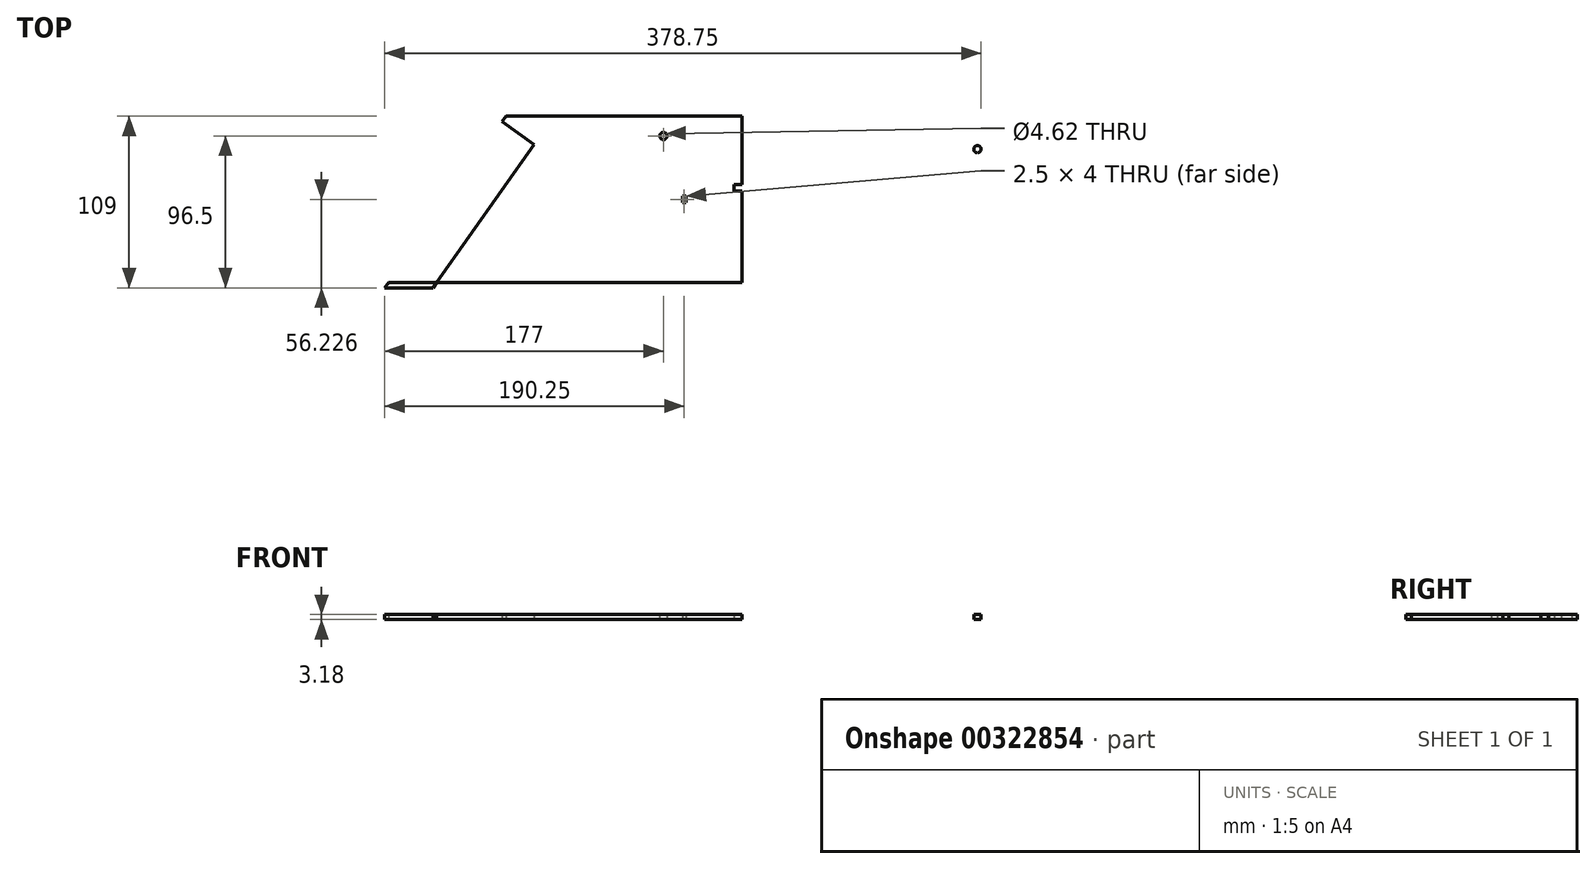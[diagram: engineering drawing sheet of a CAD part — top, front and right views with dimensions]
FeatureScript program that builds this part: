
annotation { "Feature Type Name" : "Feature", "Feature Type Description" : "" }
export const myFeature = defineFeature(function(context is Context, id is Id, definition is map)
    precondition{}
    {
        {
            var Q0;
            Q0=qCreatedBy(makeId("Top.planeOp"),FACE);
            var sketch = newSketch(context, id + "F0", { "sketchPlane" : qUnion([Q0])});
            skLineSegment(sketch, "E0.bottom", {"start": v(-423.4, 0) * mm, "end": v(-454, 0) * mm});
            skLineSegment(sketch, "E0.top", {"start": v(0, 109) * mm, "end": v(-454, 109) * mm});
            skLineSegment(sketch, "E0.left", {"start": v(0, 0) * mm, "end": v(0, 109) * mm});
            skLineSegment(sketch, "E0.right", {"start": v(-454, 0) * mm, "end": v(-454, 109) * mm});
            skLineSegment(sketch, "E1", {"start": v(-227, 109) * mm, "end": v(-77, 109) * mm});
            skLineSegment(sketch, "E2", {"start": v(-77, 109) * mm, "end": v(0, 0) * mm});
            skLineSegment(sketch, "E3", {"start": v(-227, 109) * mm, "end": v(-377, 109) * mm});
            skLineSegment(sketch, "E4", {"start": v(-377, 109) * mm, "end": v(-454, 0) * mm});
            skLineSegment(sketch, "E5.bottom", {"start": v(-177, 96.5) * mm, "end": v(-179.31, 96.5) * mm});
            skLineSegment(sketch, "E5.top", {"start": v(-177, 121.5) * mm, "end": v(-277, 121.5) * mm});
            skLineSegment(sketch, "E5.left", {"start": v(-177, 96.5) * mm, "end": v(-177, 98.81) * mm});
            skLineSegment(sketch, "E5.right", {"start": v(-277, 96.5) * mm, "end": v(-277, 98.81) * mm});
            skPoint(sketch, "E5.middle", {"position": v(-227, 109) * mm});
            skCircle(sketch, "E6", {"center": v(-277, 96.5) * mm, "radius": 2.31 * mm});
            skCircle(sketch, "E7", {"center": v(-177, 96.5) * mm, "radius": 2.31 * mm});
            skLineSegment(sketch, "E8.trimOffspring", {"start": v(-274.69, 96.5) * mm, "end": v(-277, 96.5) * mm});
            skLineSegment(sketch, "E9.trimOffspring", {"start": v(-277, 109) * mm, "end": v(-277, 121.5) * mm});
            skLineSegment(sketch, "E10.trimOffspring", {"start": v(-177, 109) * mm, "end": v(-177, 121.5) * mm});
            skLineSegment(sketch, "E11", {"start": v(-415.5, 54.5) * mm, "end": v(-386.65, 95.34) * mm});
            skLineSegment(sketch, "E12", {"start": v(-386.65, 95.34) * mm, "end": v(-435.7, 25.91) * mm});
            skLineSegment(sketch, "E13", {"start": v(-435.7, 25.91) * mm, "end": v(-425.48, 18.7) * mm});
            skLineSegment(sketch, "E14", {"start": v(-425.48, 18.7) * mm, "end": v(-376.44, 88.13) * mm});
            skLineSegment(sketch, "E15", {"start": v(-376.44, 88.13) * mm, "end": v(-386.65, 95.34) * mm});
            skCircle(sketch, "E16", {"center": v(-425.48, 18.7) * mm, "radius": 2.31 * mm});
            skCircle(sketch, "E17", {"center": v(-376.44, 88.13) * mm, "radius": 2.31 * mm});
            skLineSegment(sketch, "E18", {"start": v(-386.65, 95.34) * mm, "end": v(-379.44, 105.55) * mm});
            skLineSegment(sketch, "E19", {"start": v(-379.44, 105.55) * mm, "end": v(-359.02, 91.12) * mm});
            skLineSegment(sketch, "E20", {"start": v(-359.02, 91.12) * mm, "end": v(-423.4, 0) * mm});
            skLineSegment(sketch, "E21", {"start": v(-227, 109) * mm, "end": v(-227, 77.21) * mm});
            skCircle(sketch, "E22.MirrorC", {"center": v(-77.56, 88.13) * mm, "radius": 2.31 * mm});
            skCircle(sketch, "E23.MirrorC", {"center": v(-28.52, 18.7) * mm, "radius": 2.31 * mm});
            skLineSegment(sketch, "E24", {"start": v(-451.56, 3.45) * mm, "end": v(-2.44, 3.45) * mm});
            skLineSegment(sketch, "E25", {"start": v(-227, 109) * mm, "end": v(-227, 3.45) * mm});
            skPoint(sketch, "E26.oppositeSnap0", {"position": v(-227, 56.23) * mm});
            skLineSegment(sketch, "E26.bottom", {"start": v(-227, 56.23) * mm, "end": v(-190.25, 56.23) * mm});
            skLineSegment(sketch, "E26.top", {"start": v(-227, 56.23) * mm, "end": v(-190.25, 56.23) * mm});
            skLineSegment(sketch, "E26.left", {"start": v(-227, 56.23) * mm, "end": v(-227, 56.23) * mm});
            skLineSegment(sketch, "E26.right", {"start": v(-190.25, 56.23) * mm, "end": v(-190.25, 56.23) * mm});
            skLineSegment(sketch, "E27.bottom", {"start": v(-189, 54.23) * mm, "end": v(-191.5, 54.23) * mm});
            skLineSegment(sketch, "E27.top", {"start": v(-189, 58.23) * mm, "end": v(-191.5, 58.23) * mm});
            skLineSegment(sketch, "E27.left", {"start": v(-189, 54.23) * mm, "end": v(-189, 58.23) * mm});
            skLineSegment(sketch, "E27.right", {"start": v(-191.5, 54.23) * mm, "end": v(-191.5, 58.23) * mm});
            skPoint(sketch, "E27.middle", {"position": v(-190.25, 56.23) * mm});
            skLineSegment(sketch, "E28.MirrorCS", {"start": v(-265, 58.23) * mm, "end": v(-262.5, 58.23) * mm});
            skLineSegment(sketch, "E29.MirrorCS", {"start": v(-262.5, 54.23) * mm, "end": v(-262.5, 58.23) * mm});
            skLineSegment(sketch, "E30.MirrorCS", {"start": v(-265, 54.23) * mm, "end": v(-262.5, 54.23) * mm});
            skLineSegment(sketch, "E31.MirrorCS", {"start": v(-265, 54.23) * mm, "end": v(-265, 58.23) * mm});
            skLineSegment(sketch, "E32", {"start": v(-227, 56.23) * mm, "end": v(-227, 63.53) * mm});
            skLineSegment(sketch, "E33.bottom", {"start": v(-222, 61.53) * mm, "end": v(-232, 61.53) * mm});
            skLineSegment(sketch, "E33.top", {"start": v(-222, 65.53) * mm, "end": v(-232, 65.53) * mm});
            skLineSegment(sketch, "E33.left", {"start": v(-222, 61.53) * mm, "end": v(-222, 65.53) * mm});
            skLineSegment(sketch, "E33.right", {"start": v(-232, 61.53) * mm, "end": v(-232, 65.53) * mm});
            skPoint(sketch, "E33.middle", {"position": v(-227, 63.53) * mm});
            skSolve(sketch);
        }
        {
            var Q0;
            {var subQ11=sQuery(id+"F0.wireOp",EDGE,"E18");Q0=makeQuery(id+"F0.imprint","IMPRINT",FACE,{"disambiguationData":[TD([[makeQuery(id+"F0.imprint","IMPRINT",EDGE,{"derivedFrom":subQ11}),-1.0]])]});}
            var Q1;
            Q1=makeQuery(id+"F0.imprint","IMPRINT",FACE,{"disambiguationData":[TD([[makeQuery(id+"F0.imprint","IMPRINT",EDGE,{"derivedFrom":sQuery(id+"F0.wireOp",EDGE,"E0.bottom")}),-1.0]])]});
            var Q2;
            {var subQ1=sQuery(id+"F0.wireOp",EDGE,"E12");var subQ5=makeQuery(id+"F0.imprint","IMPRINT",VERTEX,{"derivedFrom":subQ1});Q2=makeQuery(id+"F0.imprint","IMPRINT",FACE,{"disambiguationData":[TD([[makeQuery(id+"F0.imprint","IMPRINT",EDGE,{"disambiguationData":[TD([[subQ5,1.0]])],"derivedFrom":subQ1}),1.0]])]});}
            var Q3;
            {var subQ7=sQuery(id+"F0.wireOp",EDGE,"E19");Q3=makeQuery(id+"F0.imprint","IMPRINT",FACE,{"disambiguationData":[TD([[makeQuery(id+"F0.imprint","IMPRINT",EDGE,{"derivedFrom":subQ7}),1.0]])]});}
            var Q4;
            Q4=makeQuery(id+"F0.imprint","IMPRINT",FACE,{"disambiguationData":[TD([[makeQuery(id+"F0.imprint","IMPRINT",EDGE,{"derivedFrom":sQuery(id+"F0.wireOp",EDGE,"E22.MirrorC")}),1.0]])]});
            extrude(context, id + "F1", {"entities" : qUnion([Q0, Q1, Q2, Q3, Q4]), "depth" : 3.17 * mm});
        }
    });
